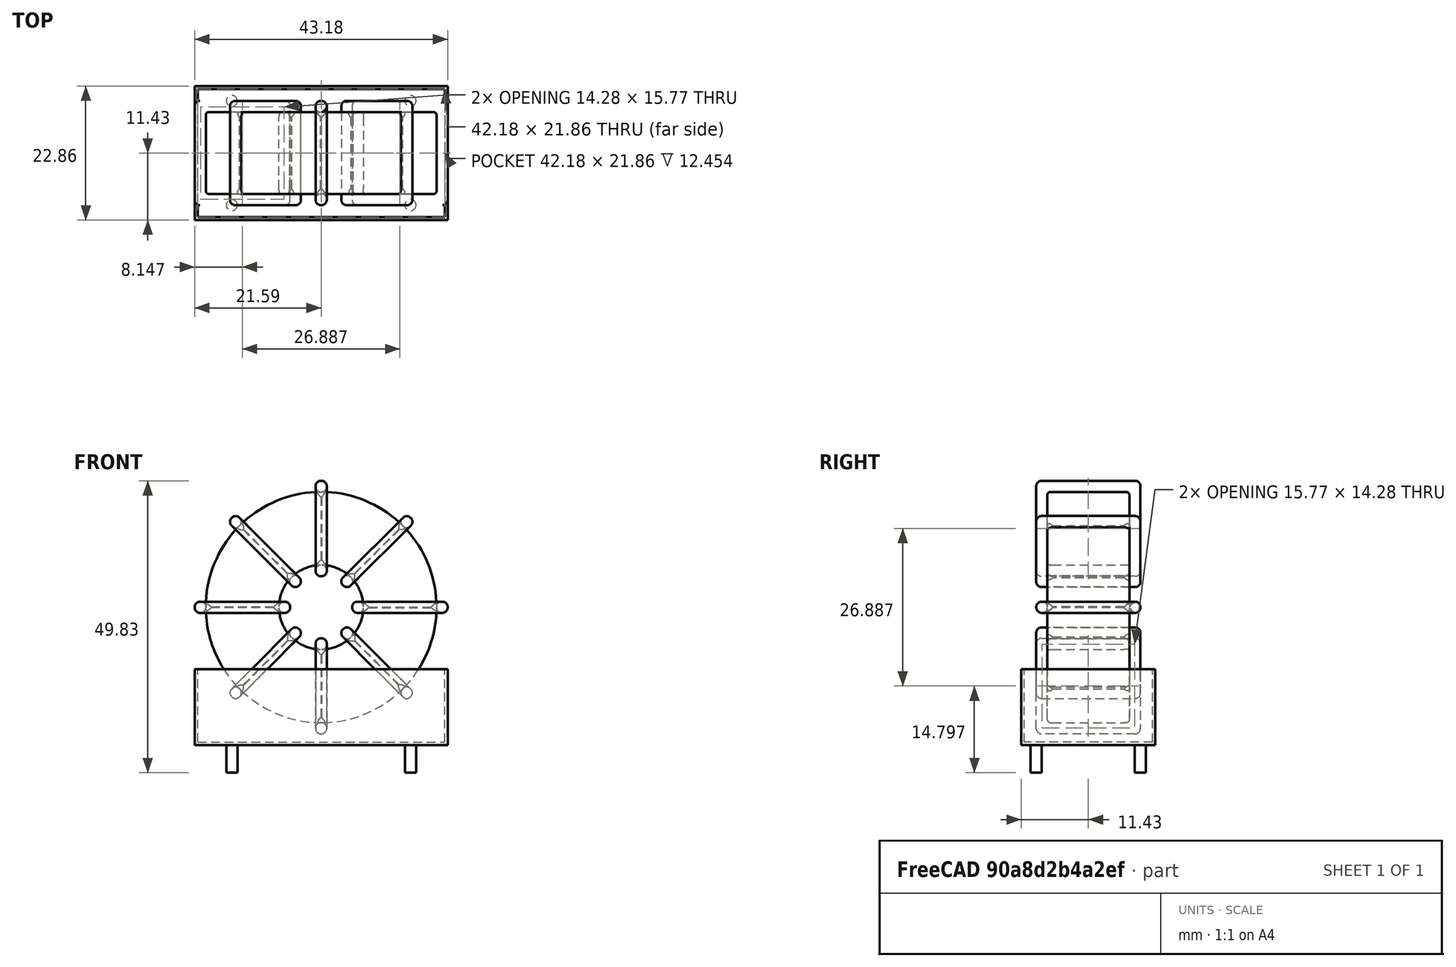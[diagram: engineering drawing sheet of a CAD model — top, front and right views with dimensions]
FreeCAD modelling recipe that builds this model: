
FCSTD DOCUMENT  (FreeCAD 0.16R6712 (Git))
Label: L_CommonMode_Toroid_Vertical_L43.2mm_W22.9mm_Px17.78mm_Py30.48mm_Bourns_8100
License: All rights reserved
LicenseURL: http://en.wikipedia.org/wiki/All_rights_reserved
objects: Sketcher::SketchObject×8, PartDesign::Pad×8, PartDesign::Fillet×5, Spreadsheet::Sheet×1, Part::MultiFuse×1
note: 30 computed .brp shape members not serialized (recipe doc carries the construction recipe); baked Part::Feature solids carry a one-line shape summary decoded from their .brp

FEATURE [Spreadsheet::Sheet] Spreadsheet  label="dimensions"
  cells = A1=Wx; B1(Wx)=43.18; C1(WW)=14.39333333333333; D1(iWx)=43.18; A2=Wy; B2(Wy)=17.78; D2(iWy)=22.86; A3=RM; B3(RMx)=17.78; C3(RMy)=30.48; A4=d_wire; B4(d_wire)=1.9; A5=H; B5(H)=31; A6=offsetx; B6(offsetx)=6.350000000000001
FEATURE [Sketcher::SketchObject] Sketch
  Placement = pos=(15.24,-8.89,0) rot=(1,0,0;1.5708rad)
  expr: Placement.Base.x = Spreadsheet.RMy / 2
  expr: Constraints[4] = Spreadsheet.WW / 2
  expr: Placement.Base.y = -Spreadsheet.RMx / 2
  expr: Constraints[0] = Spreadsheet.Wx / 2 - Spreadsheet.d_wire
  expr: Constraints[2] = Spreadsheet.Wx / 2 + Spreadsheet.d_wire + 0.5
  sketch-geometry (2):
    g0: Circle CenterX=0 CenterY=23.99 CenterZ=0 NormalX=0 NormalY=0 NormalZ=1 Radius=19.69
    g1: Circle CenterX=0 CenterY=23.99 CenterZ=0 NormalX=0 NormalY=0 NormalZ=1 Radius=7.19667
  constraints (5):
    c: Radius(g0) = 19.69
    c: DistanceX(g-1,g0) = 0
    c: DistanceY(g-1,g0) = 23.99
    c: Coincident(g1,g0)
    c: Radius(g1) = 7.19667
FEATURE [PartDesign::Pad] Pad
  Length = 13.98
  Length2 = 100
  Midplane = true
  Placement = pos=(15.24,-8.89,0) rot=(1,0,0;1.5708rad)
  Sketch = -> Sketch
  Type = 0
  expr: Length = Spreadsheet.Wy - 2 * Spreadsheet.d_wire
FEATURE [Sketcher::SketchObject] Sketch001
  Placement = pos=(0,0,0.75) rot=(0,0,1;0rad)
  expr: Constraints[4] = Spreadsheet.RMy
  expr: Constraints[2] = -Spreadsheet.RMx
  expr: Constraints[1] = Spreadsheet.d_wire / 2
  sketch-geometry (4):
    g0: Circle CenterX=0 CenterY=0 CenterZ=0 NormalX=0 NormalY=0 NormalZ=1 Radius=0.95
    g1: Circle CenterX=30.48 CenterY=-17.78 CenterZ=0 NormalX=0 NormalY=0 NormalZ=1 Radius=0.95
    g2: Circle CenterX=0 CenterY=-17.78 CenterZ=0 NormalX=0 NormalY=0 NormalZ=1 Radius=0.95
    g3: Circle CenterX=30.48 CenterY=0 CenterZ=0 NormalX=0 NormalY=0 NormalZ=1 Radius=0.95
  constraints (11):
    c: Equal(g0,g1)
    c: Radius(g0) = 0.95
    c: DistanceY(g-1,g1) = -17.78
    c: Coincident(g0,g-1)
    c: DistanceX(g-1,g1) = 30.48
    c: PointOnObject(g2,g-2)
    c: DistanceY(g-1,g3) = 0
    c: DistanceY(g2,g1) = 0
    c: DistanceX(g3,g1) = 0
    c: Equal(g3,g2)
    c: Equal(g2,g1)
FEATURE [PartDesign::Pad] Pad001
  Length = 5
  Length2 = 0
  Placement = pos=(0,0,0.75) rot=(0,0,1;0rad)
  Reversed = true
  Sketch = -> Sketch001
  Type = 0
FEATURE [PartDesign::Fillet] Fillet
  Base = -> Pad [Edge6,Edge3,Edge2]
  Placement = pos=(15.24,-8.89,0) rot=(1,0,0;1.5708rad)
  Radius = 0.5
FEATURE [Sketcher::SketchObject] Sketch003
  Placement = pos=(15.24,0,23.99) rot=(1,0,0;3.14159rad)
  expr: Placement.Base.x = Spreadsheet.RMy / 2
  expr: Constraints[18] = Spreadsheet.d_wire
  expr: Constraints[16] = Spreadsheet.d_wire
  expr: Constraints[19] = Spreadsheet.d_wire
  expr: Constraints[17] = Spreadsheet.d_wire
  expr: Placement.Base.y = -1 * (Spreadsheet.RMx - Spreadsheet.Wy) / 2
  expr: Constraints[21] = (Spreadsheet.Wx - Spreadsheet.WW) / 2 - Spreadsheet.d_wire
  expr: Constraints[22] = Spreadsheet.Wx / 2 - Spreadsheet.d_wire
  expr: Constraints[43] = Spreadsheet.d_wire
  expr: Constraints[48] = Spreadsheet.Wx - Spreadsheet.d_wire * 2
  expr: Constraints[49] = Spreadsheet.Wy
  expr: Placement.Base.z = Spreadsheet.Wx / 2 + Spreadsheet.d_wire + 0.5
  sketch-geometry (16):
    g0: LineSegment StartX=-5.29667 StartY=0 StartZ=0 EndX=-21.59 EndY=0 EndZ=0
    g1: LineSegment StartX=-21.59 StartY=0 StartZ=0 EndX=-21.59 EndY=17.78 EndZ=0
    g2: LineSegment StartX=-21.59 StartY=17.78 StartZ=0 EndX=-5.29667 EndY=17.78 EndZ=0
    g3: LineSegment StartX=-5.29667 StartY=17.78 StartZ=0 EndX=-5.29667 EndY=0 EndZ=0
    g4: LineSegment StartX=-19.69 StartY=15.88 StartZ=0 EndX=-7.19667 EndY=15.88 EndZ=0
    g5: LineSegment StartX=-7.19667 StartY=15.88 StartZ=0 EndX=-7.19667 EndY=1.9 EndZ=0
    g6: LineSegment StartX=-7.19667 StartY=1.9 StartZ=0 EndX=-19.69 EndY=1.9 EndZ=0
    g7: LineSegment StartX=-19.69 StartY=1.9 StartZ=0 EndX=-19.69 EndY=15.88 EndZ=0
    g8: LineSegment StartX=5.29667 StartY=17.78 StartZ=0 EndX=21.59 EndY=17.78 EndZ=0
    g9: LineSegment StartX=21.59 StartY=17.78 StartZ=0 EndX=21.59 EndY=0 EndZ=0
    g10: LineSegment StartX=21.59 StartY=0 StartZ=0 EndX=5.29667 EndY=0 EndZ=0
    g11: LineSegment StartX=5.29667 StartY=0 StartZ=0 EndX=5.29667 EndY=17.78 EndZ=0
    g12: LineSegment StartX=7.19667 StartY=15.88 StartZ=0 EndX=19.69 EndY=15.88 EndZ=0
    g13: LineSegment StartX=19.69 StartY=15.88 StartZ=0 EndX=19.69 EndY=1.9 EndZ=0
    g14: LineSegment StartX=19.69 StartY=1.9 StartZ=0 EndX=7.19667 EndY=1.9 EndZ=0
    g15: LineSegment StartX=7.19667 StartY=1.9 StartZ=0 EndX=7.19667 EndY=15.88 EndZ=0
  constraints (50):
    c: Horizontal(g0)
    c: Coincident(g1,g0)
    c: Vertical(g1)
    c: Coincident(g2,g1)
    c: Horizontal(g2)
    c: Coincident(g3,g2)
    c: Coincident(g3,g0)
    c: Vertical(g3)
    c: Coincident(g4,g5)
    c: Coincident(g5,g6)
    c: Coincident(g6,g7)
    c: Coincident(g7,g4)
    c: Horizontal(g4)
    c: Horizontal(g6)
    c: Vertical(g5)
    c: Vertical(g7)
    c: DistanceX(g1,g4) = 1.9
    c: DistanceY(g4,g1) = 1.9
    c: DistanceX(g5,g0) = 1.9
    c: DistanceY(g0,g5) = 1.9
    c: DistanceY(g-1,g0) = 0
    c: DistanceX(g6,g6) = 12.4933
    c: DistanceX(g6,g-1) = 19.69
    c: Coincident(g8,g9)
    c: Coincident(g9,g10)
    c: Coincident(g10,g11)
    c: Coincident(g11,g8)
    c: Horizontal(g8)
    c: Horizontal(g10)
    c: Vertical(g9)
    c: Vertical(g11)
    c: Coincident(g12,g13)
    c: Coincident(g13,g14)
    c: Coincident(g14,g15)
    c: Coincident(g15,g12)
    c: Horizontal(g12)
    c: Horizontal(g14)
    c: Vertical(g13)
    c: Vertical(g15)
    c: DistanceY(g8,g2) = 0
    c: DistanceY(g10,g0) = 0
    c: DistanceY(g14,g5) = 0
    c: DistanceY(g12,g4) = 0
    c: DistanceX(g8,g12) = 1.9
    c: Equal(g8,g2)
    c: Equal(g12,g4)
    c: Equal(g9,g1)
    c: Equal(g13,g7)
    c: DistanceX(g4,g12) = 39.38
    c: DistanceY(g0,g1) = 17.78
FEATURE [PartDesign::Pad] Pad002
  Length = 1.9
  Length2 = 100
  Midplane = true
  Placement = pos=(15.24,0,23.99) rot=(1,0,0;3.14159rad)
  Sketch = -> Sketch003
  Type = 0
  expr: Length = Spreadsheet.d_wire
FEATURE [PartDesign::Fillet] Fillet001
  Base = -> Pad002 [Edge38,Edge41,Edge42,Edge43,Edge29,Edge32,Edge33,Edge34,Edge25,Edge35,Edge36,Edge13,Edge14,Edge15,Edge16,Edge17,Edge18,Edge19,Edge1,Edge2,Edge3,Edge4,Edge5,Edge6,Edge7,Edge37,Edge39,Edge40,Edge20,Edge23,Edge24,Edge21,Edge22,Edge8,Edge9,Edge10,Edge11,Edge12,Edge26,Edge27,+8 more]
  Placement = pos=(15.24,0,23.99) rot=(1,0,0;3.14159rad)
  Radius = 0.893
  expr: Radius = Spreadsheet.d_wire * 0.47
FEATURE [Sketcher::SketchObject] Sketch004
  Placement = pos=(15.24,0,23.99) rot=(0.92388,0,0.382683;3.14159rad)
  expr: Placement.Base.x = Spreadsheet.RMy / 2
  expr: Constraints[18] = Spreadsheet.d_wire
  expr: Constraints[16] = Spreadsheet.d_wire
  expr: Constraints[19] = Spreadsheet.d_wire
  expr: Constraints[17] = Spreadsheet.d_wire
  expr: Placement.Base.y = -1 * (Spreadsheet.RMx - Spreadsheet.Wy) / 2
  expr: Constraints[21] = (Spreadsheet.Wx - Spreadsheet.WW) / 2 - Spreadsheet.d_wire
  expr: Constraints[22] = Spreadsheet.Wx / 2 - Spreadsheet.d_wire
  expr: Constraints[43] = Spreadsheet.d_wire
  expr: Constraints[48] = Spreadsheet.Wx - 2 * Spreadsheet.d_wire
  expr: Constraints[49] = Spreadsheet.Wy
  expr: Placement.Base.z = Spreadsheet.Wx / 2 + Spreadsheet.d_wire + 0.5
  sketch-geometry (16):
    g0: LineSegment StartX=-5.29667 StartY=0 StartZ=0 EndX=-21.59 EndY=0 EndZ=0
    g1: LineSegment StartX=-21.59 StartY=0 StartZ=0 EndX=-21.59 EndY=17.78 EndZ=0
    g2: LineSegment StartX=-21.59 StartY=17.78 StartZ=0 EndX=-5.29667 EndY=17.78 EndZ=0
    g3: LineSegment StartX=-5.29667 StartY=17.78 StartZ=0 EndX=-5.29667 EndY=0 EndZ=0
    g4: LineSegment StartX=-19.69 StartY=15.88 StartZ=0 EndX=-7.19667 EndY=15.88 EndZ=0
    g5: LineSegment StartX=-7.19667 StartY=15.88 StartZ=0 EndX=-7.19667 EndY=1.9 EndZ=0
    g6: LineSegment StartX=-7.19667 StartY=1.9 StartZ=0 EndX=-19.69 EndY=1.9 EndZ=0
    g7: LineSegment StartX=-19.69 StartY=1.9 StartZ=0 EndX=-19.69 EndY=15.88 EndZ=0
    g8: LineSegment StartX=5.29667 StartY=17.78 StartZ=0 EndX=21.59 EndY=17.78 EndZ=0
    g9: LineSegment StartX=21.59 StartY=17.78 StartZ=0 EndX=21.59 EndY=0 EndZ=0
    g10: LineSegment StartX=21.59 StartY=0 StartZ=0 EndX=5.29667 EndY=0 EndZ=0
    g11: LineSegment StartX=5.29667 StartY=0 StartZ=0 EndX=5.29667 EndY=17.78 EndZ=0
    g12: LineSegment StartX=7.19667 StartY=15.88 StartZ=0 EndX=19.69 EndY=15.88 EndZ=0
    g13: LineSegment StartX=19.69 StartY=15.88 StartZ=0 EndX=19.69 EndY=1.9 EndZ=0
    g14: LineSegment StartX=19.69 StartY=1.9 StartZ=0 EndX=7.19667 EndY=1.9 EndZ=0
    g15: LineSegment StartX=7.19667 StartY=1.9 StartZ=0 EndX=7.19667 EndY=15.88 EndZ=0
  constraints (50):
    c: Horizontal(g0)
    c: Coincident(g1,g0)
    c: Vertical(g1)
    c: Coincident(g2,g1)
    c: Horizontal(g2)
    c: Coincident(g3,g2)
    c: Coincident(g3,g0)
    c: Vertical(g3)
    c: Coincident(g4,g5)
    c: Coincident(g5,g6)
    c: Coincident(g6,g7)
    c: Coincident(g7,g4)
    c: Horizontal(g4)
    c: Horizontal(g6)
    c: Vertical(g5)
    c: Vertical(g7)
    c: DistanceX(g1,g4) = 1.9
    c: DistanceY(g4,g1) = 1.9
    c: DistanceX(g5,g0) = 1.9
    c: DistanceY(g0,g5) = 1.9
    c: DistanceY(g-1,g0) = 0
    c: DistanceX(g6,g6) = 12.4933
    c: DistanceX(g6,g-1) = 19.69
    c: Coincident(g8,g9)
    c: Coincident(g9,g10)
    c: Coincident(g10,g11)
    c: Coincident(g11,g8)
    c: Horizontal(g8)
    c: Horizontal(g10)
    c: Vertical(g9)
    c: Vertical(g11)
    c: Coincident(g12,g13)
    c: Coincident(g13,g14)
    c: Coincident(g14,g15)
    c: Coincident(g15,g12)
    c: Horizontal(g12)
    c: Horizontal(g14)
    c: Vertical(g13)
    c: Vertical(g15)
    c: DistanceY(g8,g2) = 0
    c: DistanceY(g10,g0) = 0
    c: DistanceY(g14,g5) = 0
    c: DistanceY(g12,g4) = 0
    c: DistanceX(g8,g12) = 1.9
    c: Equal(g8,g2)
    c: Equal(g12,g4)
    c: Equal(g9,g1)
    c: Equal(g13,g7)
    c: DistanceX(g4,g12) = 39.38
    c: DistanceY(g0,g1) = 17.78
FEATURE [PartDesign::Pad] Pad003
  Length = 1.9
  Length2 = 100
  Midplane = true
  Placement = pos=(15.24,0,23.99) rot=(0.92388,0,0.382683;3.14159rad)
  Sketch = -> Sketch004
  Type = 0
  expr: Length = Spreadsheet.d_wire
FEATURE [PartDesign::Fillet] Fillet002
  Base = -> Pad003 [Edge38,Edge41,Edge42,Edge43,Edge29,Edge32,Edge33,Edge34,Edge25,Edge35,Edge36,Edge13,Edge14,Edge15,Edge16,Edge17,Edge18,Edge19,Edge1,Edge2,Edge3,Edge4,Edge5,Edge6,Edge7,Edge37,Edge39,Edge40,Edge20,Edge23,Edge24,Edge21,Edge22,Edge8,Edge9,Edge10,Edge11,Edge12,Edge26,Edge27,+8 more]
  Placement = pos=(15.24,0,23.99) rot=(0.92388,0,0.382683;3.14159rad)
  Radius = 0.893
  expr: Radius = Spreadsheet.d_wire * 0.47
FEATURE [Sketcher::SketchObject] Sketch005
  Placement = pos=(15.24,0,23.99) rot=(0.92388,0,-0.382683;3.14159rad)
  expr: Placement.Base.x = Spreadsheet.RMy / 2
  expr: Constraints[18] = Spreadsheet.d_wire
  expr: Constraints[16] = Spreadsheet.d_wire
  expr: Constraints[19] = Spreadsheet.d_wire
  expr: Constraints[17] = Spreadsheet.d_wire
  expr: Placement.Base.y = -1 * (Spreadsheet.RMx - Spreadsheet.Wy) / 2
  expr: Constraints[21] = (Spreadsheet.Wx - Spreadsheet.WW) / 2 - Spreadsheet.d_wire
  expr: Constraints[22] = Spreadsheet.Wx / 2 - Spreadsheet.d_wire
  expr: Constraints[43] = Spreadsheet.d_wire
  expr: Constraints[48] = Spreadsheet.Wx - 2 * Spreadsheet.d_wire
  expr: Constraints[49] = Spreadsheet.Wy
  expr: Placement.Base.z = Spreadsheet.Wx / 2 + Spreadsheet.d_wire + 0.5
  sketch-geometry (16):
    g0: LineSegment StartX=-5.29667 StartY=0 StartZ=0 EndX=-21.59 EndY=0 EndZ=0
    g1: LineSegment StartX=-21.59 StartY=0 StartZ=0 EndX=-21.59 EndY=17.78 EndZ=0
    g2: LineSegment StartX=-21.59 StartY=17.78 StartZ=0 EndX=-5.29667 EndY=17.78 EndZ=0
    g3: LineSegment StartX=-5.29667 StartY=17.78 StartZ=0 EndX=-5.29667 EndY=0 EndZ=0
    g4: LineSegment StartX=-19.69 StartY=15.88 StartZ=0 EndX=-7.19667 EndY=15.88 EndZ=0
    g5: LineSegment StartX=-7.19667 StartY=15.88 StartZ=0 EndX=-7.19667 EndY=1.9 EndZ=0
    g6: LineSegment StartX=-7.19667 StartY=1.9 StartZ=0 EndX=-19.69 EndY=1.9 EndZ=0
    g7: LineSegment StartX=-19.69 StartY=1.9 StartZ=0 EndX=-19.69 EndY=15.88 EndZ=0
    g8: LineSegment StartX=5.29667 StartY=17.78 StartZ=0 EndX=21.59 EndY=17.78 EndZ=0
    g9: LineSegment StartX=21.59 StartY=17.78 StartZ=0 EndX=21.59 EndY=0 EndZ=0
    g10: LineSegment StartX=21.59 StartY=0 StartZ=0 EndX=5.29667 EndY=0 EndZ=0
    g11: LineSegment StartX=5.29667 StartY=0 StartZ=0 EndX=5.29667 EndY=17.78 EndZ=0
    g12: LineSegment StartX=7.19667 StartY=15.88 StartZ=0 EndX=19.69 EndY=15.88 EndZ=0
    g13: LineSegment StartX=19.69 StartY=15.88 StartZ=0 EndX=19.69 EndY=1.9 EndZ=0
    g14: LineSegment StartX=19.69 StartY=1.9 StartZ=0 EndX=7.19667 EndY=1.9 EndZ=0
    g15: LineSegment StartX=7.19667 StartY=1.9 StartZ=0 EndX=7.19667 EndY=15.88 EndZ=0
  constraints (50):
    c: Horizontal(g0)
    c: Coincident(g1,g0)
    c: Vertical(g1)
    c: Coincident(g2,g1)
    c: Horizontal(g2)
    c: Coincident(g3,g2)
    c: Coincident(g3,g0)
    c: Vertical(g3)
    c: Coincident(g4,g5)
    c: Coincident(g5,g6)
    c: Coincident(g6,g7)
    c: Coincident(g7,g4)
    c: Horizontal(g4)
    c: Horizontal(g6)
    c: Vertical(g5)
    c: Vertical(g7)
    c: DistanceX(g1,g4) = 1.9
    c: DistanceY(g4,g1) = 1.9
    c: DistanceX(g5,g0) = 1.9
    c: DistanceY(g0,g5) = 1.9
    c: DistanceY(g-1,g0) = 0
    c: DistanceX(g6,g6) = 12.4933
    c: DistanceX(g6,g-1) = 19.69
    c: Coincident(g8,g9)
    c: Coincident(g9,g10)
    c: Coincident(g10,g11)
    c: Coincident(g11,g8)
    c: Horizontal(g8)
    c: Horizontal(g10)
    c: Vertical(g9)
    c: Vertical(g11)
    c: Coincident(g12,g13)
    c: Coincident(g13,g14)
    c: Coincident(g14,g15)
    c: Coincident(g15,g12)
    c: Horizontal(g12)
    c: Horizontal(g14)
    c: Vertical(g13)
    c: Vertical(g15)
    c: DistanceY(g8,g2) = 0
    c: DistanceY(g10,g0) = 0
    c: DistanceY(g14,g5) = 0
    c: DistanceY(g12,g4) = 0
    c: DistanceX(g8,g12) = 1.9
    c: Equal(g8,g2)
    c: Equal(g12,g4)
    c: Equal(g9,g1)
    c: Equal(g13,g7)
    c: DistanceX(g4,g12) = 39.38
    c: DistanceY(g0,g1) = 17.78
FEATURE [PartDesign::Pad] Pad004
  Length = 1.9
  Length2 = 100
  Midplane = true
  Placement = pos=(15.24,0,23.99) rot=(0.92388,0,-0.382683;3.14159rad)
  Sketch = -> Sketch005
  Type = 0
  expr: Length = Spreadsheet.d_wire
FEATURE [PartDesign::Fillet] Fillet003
  Base = -> Pad004 [Edge38,Edge41,Edge42,Edge43,Edge29,Edge32,Edge33,Edge34,Edge25,Edge35,Edge36,Edge13,Edge14,Edge15,Edge16,Edge17,Edge18,Edge19,Edge1,Edge2,Edge3,Edge4,Edge5,Edge6,Edge7,Edge37,Edge39,Edge40,Edge20,Edge23,Edge24,Edge21,Edge22,Edge8,Edge9,Edge10,Edge11,Edge12,Edge26,Edge27,+8 more]
  Placement = pos=(15.24,0,23.99) rot=(0.92388,0,-0.382683;3.14159rad)
  Radius = 0.893
  expr: Radius = Spreadsheet.d_wire * 0.47
FEATURE [Sketcher::SketchObject] Sketch006
  Placement = pos=(15.24,0,23.99) rot=(0.707107,0,0.707107;3.14159rad)
  expr: Placement.Base.x = Spreadsheet.RMy / 2
  expr: Constraints[18] = Spreadsheet.d_wire
  expr: Constraints[16] = Spreadsheet.d_wire
  expr: Constraints[19] = Spreadsheet.d_wire
  expr: Constraints[17] = Spreadsheet.d_wire
  expr: Placement.Base.y = -1 * (Spreadsheet.RMx - Spreadsheet.Wy) / 2
  expr: Constraints[21] = (Spreadsheet.Wx - Spreadsheet.WW) / 2 - Spreadsheet.d_wire
  expr: Constraints[22] = Spreadsheet.Wx / 2 - Spreadsheet.d_wire
  expr: Constraints[43] = Spreadsheet.d_wire
  expr: Constraints[48] = Spreadsheet.Wx - Spreadsheet.d_wire * 2
  expr: Constraints[49] = Spreadsheet.Wy
  expr: Placement.Base.z = Spreadsheet.Wx / 2 + Spreadsheet.d_wire + 0.5
  sketch-geometry (16):
    g0: LineSegment StartX=-5.29667 StartY=0 StartZ=0 EndX=-21.59 EndY=0 EndZ=0
    g1: LineSegment StartX=-21.59 StartY=0 StartZ=0 EndX=-21.59 EndY=17.78 EndZ=0
    g2: LineSegment StartX=-21.59 StartY=17.78 StartZ=0 EndX=-5.29667 EndY=17.78 EndZ=0
    g3: LineSegment StartX=-5.29667 StartY=17.78 StartZ=0 EndX=-5.29667 EndY=0 EndZ=0
    g4: LineSegment StartX=-19.69 StartY=15.88 StartZ=0 EndX=-7.19667 EndY=15.88 EndZ=0
    g5: LineSegment StartX=-7.19667 StartY=15.88 StartZ=0 EndX=-7.19667 EndY=1.9 EndZ=0
    g6: LineSegment StartX=-7.19667 StartY=1.9 StartZ=0 EndX=-19.69 EndY=1.9 EndZ=0
    g7: LineSegment StartX=-19.69 StartY=1.9 StartZ=0 EndX=-19.69 EndY=15.88 EndZ=0
    g8: LineSegment StartX=5.29667 StartY=17.78 StartZ=0 EndX=21.59 EndY=17.78 EndZ=0
    g9: LineSegment StartX=21.59 StartY=17.78 StartZ=0 EndX=21.59 EndY=0 EndZ=0
    g10: LineSegment StartX=21.59 StartY=0 StartZ=0 EndX=5.29667 EndY=0 EndZ=0
    g11: LineSegment StartX=5.29667 StartY=0 StartZ=0 EndX=5.29667 EndY=17.78 EndZ=0
    g12: LineSegment StartX=7.19667 StartY=15.88 StartZ=0 EndX=19.69 EndY=15.88 EndZ=0
    g13: LineSegment StartX=19.69 StartY=15.88 StartZ=0 EndX=19.69 EndY=1.9 EndZ=0
    g14: LineSegment StartX=19.69 StartY=1.9 StartZ=0 EndX=7.19667 EndY=1.9 EndZ=0
    g15: LineSegment StartX=7.19667 StartY=1.9 StartZ=0 EndX=7.19667 EndY=15.88 EndZ=0
  constraints (50):
    c: Horizontal(g0)
    c: Coincident(g1,g0)
    c: Vertical(g1)
    c: Coincident(g2,g1)
    c: Horizontal(g2)
    c: Coincident(g3,g2)
    c: Coincident(g3,g0)
    c: Vertical(g3)
    c: Coincident(g4,g5)
    c: Coincident(g5,g6)
    c: Coincident(g6,g7)
    c: Coincident(g7,g4)
    c: Horizontal(g4)
    c: Horizontal(g6)
    c: Vertical(g5)
    c: Vertical(g7)
    c: DistanceX(g1,g4) = 1.9
    c: DistanceY(g4,g1) = 1.9
    c: DistanceX(g5,g0) = 1.9
    c: DistanceY(g0,g5) = 1.9
    c: DistanceY(g-1,g0) = 0
    c: DistanceX(g6,g6) = 12.4933
    c: DistanceX(g6,g-1) = 19.69
    c: Coincident(g8,g9)
    c: Coincident(g9,g10)
    c: Coincident(g10,g11)
    c: Coincident(g11,g8)
    c: Horizontal(g8)
    c: Horizontal(g10)
    c: Vertical(g9)
    c: Vertical(g11)
    c: Coincident(g12,g13)
    c: Coincident(g13,g14)
    c: Coincident(g14,g15)
    c: Coincident(g15,g12)
    c: Horizontal(g12)
    c: Horizontal(g14)
    c: Vertical(g13)
    c: Vertical(g15)
    c: DistanceY(g8,g2) = 0
    c: DistanceY(g10,g0) = 0
    c: DistanceY(g14,g5) = 0
    c: DistanceY(g12,g4) = 0
    c: DistanceX(g8,g12) = 1.9
    c: Equal(g8,g2)
    c: Equal(g12,g4)
    c: Equal(g9,g1)
    c: Equal(g13,g7)
    c: DistanceX(g4,g12) = 39.38
    c: DistanceY(g0,g1) = 17.78
FEATURE [PartDesign::Pad] Pad005
  Length = 1.9
  Length2 = 100
  Midplane = true
  Placement = pos=(15.24,0,23.99) rot=(0.707107,0,0.707107;3.14159rad)
  Sketch = -> Sketch006
  Type = 0
  expr: Length = Spreadsheet.d_wire
FEATURE [PartDesign::Fillet] Fillet004
  Base = -> Pad005 [Edge38,Edge41,Edge42,Edge43,Edge29,Edge32,Edge33,Edge34,Edge25,Edge35,Edge36,Edge13,Edge14,Edge15,Edge16,Edge17,Edge18,Edge19,Edge1,Edge2,Edge3,Edge4,Edge5,Edge6,Edge7,Edge37,Edge39,Edge40,Edge20,Edge23,Edge24,Edge21,Edge22,Edge8,Edge9,Edge10,Edge11,Edge12,Edge26,Edge27,+8 more]
  Placement = pos=(15.24,0,23.99) rot=(0.707107,0,0.707107;3.14159rad)
  Radius = 0.893
  expr: Radius = Spreadsheet.d_wire * 0.47
FEATURE [Sketcher::SketchObject] Sketch007
  Placement = pos=(15.24,0,0.5) rot=(0,0,1;0rad)
  expr: Placement.Base.x = Spreadsheet.RMy / 2
  expr: Placement.Base.z = 0.5
  expr: Constraints[11] = Spreadsheet.iWx / 2
  expr: Constraints[10] = (Spreadsheet.iWy - Spreadsheet.RMx) / 2
  expr: Constraints[9] = Spreadsheet.iWy
  expr: Constraints[8] = Spreadsheet.iWx
  sketch-geometry (4):
    g0: LineSegment StartX=-21.59 StartY=2.54 StartZ=0 EndX=21.59 EndY=2.54 EndZ=0
    g1: LineSegment StartX=21.59 StartY=2.54 StartZ=0 EndX=21.59 EndY=-20.32 EndZ=0
    g2: LineSegment StartX=21.59 StartY=-20.32 StartZ=0 EndX=-21.59 EndY=-20.32 EndZ=0
    g3: LineSegment StartX=-21.59 StartY=-20.32 StartZ=0 EndX=-21.59 EndY=2.54 EndZ=0
  constraints (12):
    c: Coincident(g0,g1)
    c: Coincident(g1,g2)
    c: Coincident(g2,g3)
    c: Coincident(g3,g0)
    c: Horizontal(g0)
    c: Horizontal(g2)
    c: Vertical(g1)
    c: Vertical(g3)
    c: DistanceX(g0,g0) = 43.18
    c: DistanceY(g3,g3) = 22.86
    c: DistanceY(g-1,g0) = 2.54
    c: DistanceX(g0,g-1) = 21.59
FEATURE [PartDesign::Pad] Pad006
  Length = 0.5
  Length2 = 100
  Placement = pos=(15.24,0,0.5) rot=(0,0,1;0rad)
  Sketch = -> Sketch007
  Type = 0
FEATURE [Sketcher::SketchObject] Sketch008
  Placement = pos=(15.24,0,0.5) rot=(0,0,1;0rad)
  expr: Placement.Base.x = Spreadsheet.RMy / 2
  expr: Constraints[8] = Spreadsheet.iWx
  expr: Constraints[9] = Spreadsheet.iWy
  expr: Constraints[10] = (Spreadsheet.iWy - Spreadsheet.RMx) / 2
  expr: Placement.Base.z = 0.5
  expr: Constraints[21] = 0.5
  expr: Constraints[11] = Spreadsheet.iWx / 2
  sketch-geometry (8):
    g0: LineSegment StartX=-21.59 StartY=2.54 StartZ=0 EndX=21.59 EndY=2.54 EndZ=0
    g1: LineSegment StartX=21.59 StartY=2.54 StartZ=0 EndX=21.59 EndY=-20.32 EndZ=0
    g2: LineSegment StartX=21.59 StartY=-20.32 StartZ=0 EndX=-21.59 EndY=-20.32 EndZ=0
    g3: LineSegment StartX=-21.59 StartY=-20.32 StartZ=0 EndX=-21.59 EndY=2.54 EndZ=0
    g4: LineSegment StartX=-21.09 StartY=2.04 StartZ=0 EndX=21.09 EndY=2.04 EndZ=0
    g5: LineSegment StartX=21.09 StartY=2.04 StartZ=0 EndX=21.09 EndY=-19.82 EndZ=0
    g6: LineSegment StartX=21.09 StartY=-19.82 StartZ=0 EndX=-21.09 EndY=-19.82 EndZ=0
    g7: LineSegment StartX=-21.09 StartY=-19.82 StartZ=0 EndX=-21.09 EndY=2.04 EndZ=0
  constraints (24):
    c: Coincident(g0,g1)
    c: Coincident(g1,g2)
    c: Coincident(g2,g3)
    c: Coincident(g3,g0)
    c: Horizontal(g0)
    c: Horizontal(g2)
    c: Vertical(g1)
    c: Vertical(g3)
    c: DistanceX(g0,g0) = 43.18
    c: DistanceY(g3,g3) = 22.86
    c: DistanceY(g-1,g0) = 2.54
    c: DistanceX(g0,g-1) = 21.59
    c: Coincident(g4,g5)
    c: Coincident(g5,g6)
    c: Coincident(g6,g7)
    c: Coincident(g7,g4)
    c: Horizontal(g4)
    c: Horizontal(g6)
    c: Vertical(g5)
    c: Vertical(g7)
    c: DistanceX(g5,g1) = 0.5
    c: DistanceY(g1,g5) = 0.5
    c: DistanceX(g0,g4) = 0.5
    c: DistanceY(g4,g0) = 0.5
FEATURE [PartDesign::Pad] Pad007
  Length = 12.954
  Length2 = 100
  Placement = pos=(15.24,0,0.5) rot=(0,0,1;0rad)
  Sketch = -> Sketch008
  Type = 0
  expr: Length = Spreadsheet.Wx * 0.3
FEATURE [Part::MultiFuse] Fillet002_mp_cp  label="L_CommonMode_Toroid_Vertical_L43.2mm_W22.9mm_Px17.78mm_Py30.48mm_Bourns_8100"
  Shapes = -> [Fillet002,Fillet001,Fillet,Pad001,Pad007,Pad006,Fillet004,Fillet003]
